# Revit family: Lighting_Desk&Table_Nordlux_Glossy
name_source: partatom
category: Lighting Fixtures
revit_build: Autodesk Revit 2017 (Build: 20160225_1515(x64)
units: mm (PartAtom-declared; Revit-internal decimal feet)

## family parameters
Always vertical = Yes
Cut with Voids When Loaded = No
Light Source = Yes
OmniClass Number = 23.80.70.00
OmniClass Title = Lighting
Part Type = Normal
Room Calculation Point = No
Round Connector Dimension = Use Diameter
Shared = No
Work Plane-Based = No

## types (1)
- Glossy
    ArticleNumber = 2020505001
    AssetType = Fixed
    BIMObjectName = Lighting_Desk&Table_Nordlux_Glossy
    Brand = Nordlux
    Category = Table lighting
    Collection = Glossy
    Color = Opal white
    Color Filter = 16777215
    ConvergoRefNr = 0143-2009-0010-DK
    DefaultElevation = 0 mm  [stored 0 ft]
    Description = Glossy is the epitome of tasteful and sophisticated design. The Danish designer, Maria Berntsen, has created a table lamp that oozes of Nordic minimalism, and where the combination of the exclusive materials, marble, brass and opal white glass contribute to an incredibly elegant design. Glossy is named after the shiny surface of the opal white glass, which lets a soft and comfortable light shine through.
    Designer = Maria Berntsen
    Dimming Lamp Color Temperature Shift = <None>
    DurationUnit = Hours
    EANNumber = 5704924001024
    ElectricalDeviceNominalPower = 15
    Emit Shape Visible in Rendering = No
    Emit from Circle Diameter = 50 mm  [stored 0.164042 ft]
    Features = Cable length: 250 cm. Socket type E27. Light source not included. Energy class A++ - A.
    Finish = Cable colour: White textile cable
    HasProtectiveEarth = Yes
    IP_Code = IP20
    IfcExportAs = IfcLightFixtureType
    IfcExportType = NOTDEFINED
    InsulationStandardClass = Class 2 (Double isolated)
    LensMaterial = Glass
    LightFixtureMainMaterial = Marble
    LightFixtureMountingType = FreeStanding
    LightFixturePlacingType = Furniture
    MaintenanceFactor = 0
    Manufacturer = Nordlux
    ManufacturerName = Nordlux
    ManufacturerURL = https://www.nordlux.com
    Material = Marble & Glass
    Model = Glossy
    ModelReference = 2020505001
    NBSDescription = General purpose luminaires
    NBSReference = 90-60-50/405
    Name = Glossy
    NominalCurrent = 0 A
    NominalDiameter = 320 mm  [stored 1.04987 ft]
    NominalFrequencyRange = 50 Hz
    NominalHeight = 316 mm
    NominalLength = 324 mm
    NominalRadius = 160 mm  [stored 0.524934 ft]
    NominalVoltage = 230 V
    NominalVoltageCalc = 230 V
    NominalWidth = 324 mm
    NumberOfPoles = 1
    NumberOfSources = 0
    PhaseAngle = 0.00°
    Photometric Web File = 2020505001 Glossy Table.ies
    ProductDatasheet = http://pim.skypim.com
    ProductInformation = Glossy is the epitome of tasteful and sophisticated design. The Danish designer, Maria Berntsen, has created a table lamp that oozes of Nordic minimalism, and where the combination of the exclusive materials, marble, brass and opal white glass contribute to an incredibly elegant design. Glossy is named after the shiny surface of the opal white glass, which lets a soft and comfortable light shine through.
    Shape = Sculptured
    Size = 320x320x320 mm
    Tilt Angle = 90.00°
    TotalWattage = 15 W
    URL = https://www.nordlux.com
    Uniclass2 = Pr_70_70_49_43
    Uniclass2015Description = Light-Emitting Diode (LED) Luminaires
    Uniclass2015Reference = Pr_70_70_48_46
    UsageCurrent = 0 A
    Version = 1
    VersionDate = 24/11/2020
    WarrantyDurationUnit = Hours

note: [stored X ft] marks values corroborated as IEEE doubles in the binary element streams (Revit-internal decimal feet)

## geometry (parser evidence)
native form markers: Sweep x5
no freeform markers — native parametric forms only
